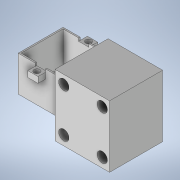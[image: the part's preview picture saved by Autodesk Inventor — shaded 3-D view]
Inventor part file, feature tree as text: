
AUTODESK INVENTOR PART (.ipt)
format: ipt  version: 2020.2 (Build 242310000, 310)  size: 366,592 bytes
history: native  units: in
note: dims shown in document units (in); Inventor stores cm internally (conversion verified against a paired STEP export)
features: sketch x10, extrude x9, projected_geometry x4, hole x1
ambient origin geometry x8: Origin, YZ Plane, XZ Plane, XY Plane, X Axis, Y Axis, Z Axis, Center Point
bodies: Solid1 (feature_tree)
feature tree (24):
  extrude  "Extrusion1"  TaperAngle=180.0deg  [1 undecoded]
  extrude  "Extrusion3"  Depth=0.0787in TaperAngle=0.0deg
  extrude  "Extrusion4"  Depth=0.0394in
  extrude  "Extrusion5"  Depth=0.0394in
  extrude  "Extrusion6"  Depth=0.3126in
  extrude  "Extrusion32"  Depth=0.0787in TaperAngle=0.0deg
  hole  "Hole3"  [1 undecoded]
  sketch  "Sketch37"  dims[d19=1.378in d20=0.1575in]
  sketch  "Sketch38"  dims[d21=0.1575in d22=0.1378in]
  extrude  "Extrusion33"  Depth=0.1575in
  extrude  "Extrusion37"  Depth=0.1378in
  extrude  "Extrusion38"  Depth=0.2756in
  sketch  "Sketch1"  dims[d0=1.2599in d1=180.0deg]
  sketch  "Sketch2"  dims[d2=1.2in d3=0.0787in d4=0.0in]
  projected_geometry  "Projected Loop1"
  sketch  "Sketch3"  dims[d5=0.0394in d6=0.0394in]
  sketch  "Sketch4"  dims[d7=0.0394in d8=0.0394in]
  sketch  "Sketch5"  dims[d11=0.3126in d12=0.3126in]
  projected_geometry  "Projected Loop2"
  sketch  "Sketch35"  dims[d13=0.7874in d14=0.0in d15=0.0787in d16=0.0in]
  sketch  "Sketch36"  dims[d17=0.6693in d18=0.689in]
  projected_geometry  "Projected Loop14"
  sketch  "Sketch42"  dims[d23=0.1969in d24=0.2756in d25=0.1969in d26=0.1575in d27=0.0in d28=0.0787in d29=0.0in d177=0.7874in d178=1.378in d179=1.5748in d180=0.0394in d181=0.0in d182=0.1969in d183=0.1969in d184=1.1654in d185=1.0256in d186=1.1654in d187=90.0deg d188=0.1339in d189=0.2362in d190=0.1575in d191=0.0787in d192=90.0deg d193=0.315in d194=0.8108in d195=0.0394in d196=0.3543in d197=1.4567in d198=1.6535in d199=0.0394in d200=0.0394in d201=0.0394in d202=1.1811in d203=0.0in d224=0.2756in d225=0.2756in d226=0.2756in d227=0.2756in d228=0.2362in d229=0.0in d230=0.315in d231=0.0in]
  projected_geometry  "Projected Loop15"
note: 2 required parameter values undecoded (feature->parameter linkage not recoverable at this tier; creation-order binding heuristic only, values carry confidence <= 0.55)
